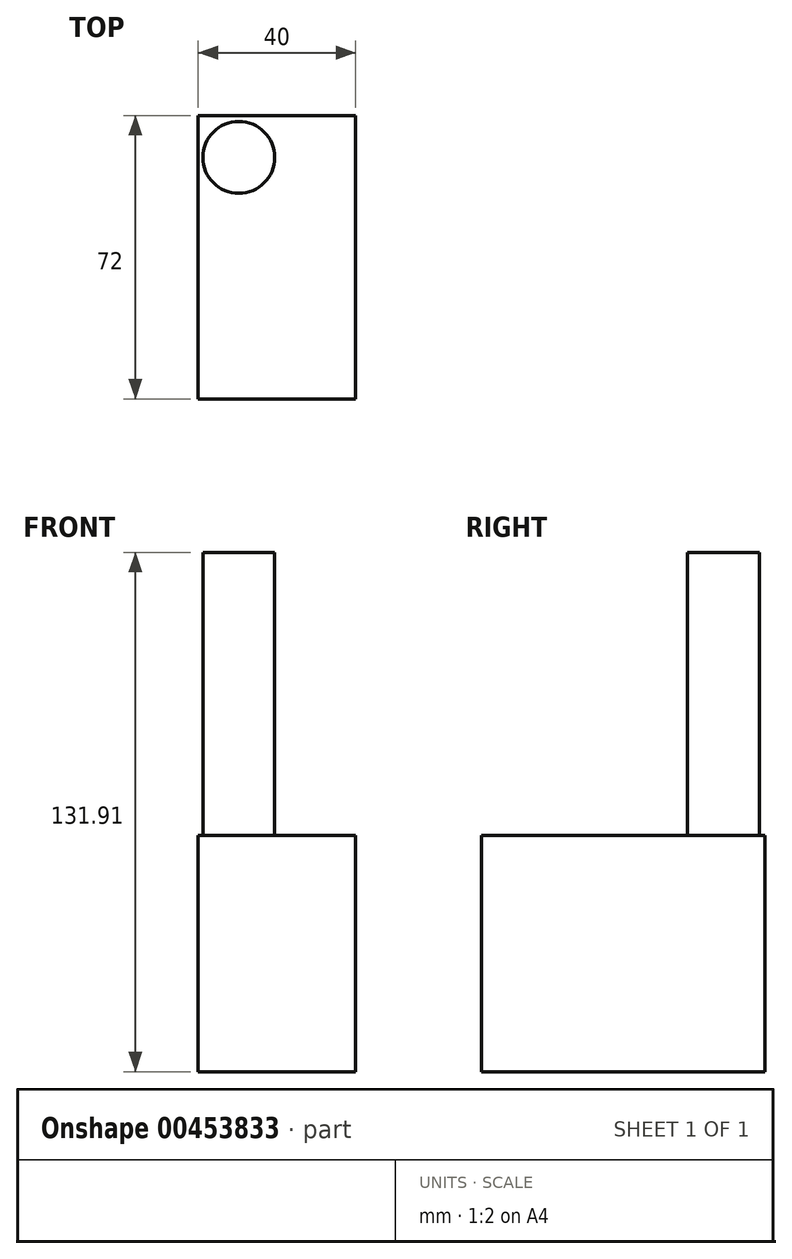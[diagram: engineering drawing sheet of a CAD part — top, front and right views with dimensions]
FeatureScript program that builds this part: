
annotation { "Feature Type Name" : "Feature", "Feature Type Description" : "" }
export const myFeature = defineFeature(function(context is Context, id is Id, definition is map)
    precondition{}
    {
        {
            var Q0;
            Q0=qCreatedBy(makeId("Front.planeOp"),FACE);
            var sketch = newSketch(context, id + "F0", { "sketchPlane" : qUnion([Q0])});
            skLineSegment(sketch, "E0.bottom", {"start": v(-20, 30) * mm, "end": v(20, 30) * mm});
            skLineSegment(sketch, "E0.top", {"start": v(-20, -30) * mm, "end": v(20, -30) * mm});
            skLineSegment(sketch, "E0.left", {"start": v(-20, 30) * mm, "end": v(-20, -30) * mm});
            skLineSegment(sketch, "E0.right", {"start": v(20, 30) * mm, "end": v(20, -30) * mm});
            skPoint(sketch, "E0.middle", {"position": v(0, 0) * mm});
            skSolve(sketch);
        }
        {
            var Q0;
            Q0=makeQuery(id+"F0.imprint","IMPRINT",FACE,{"disambiguationData":[TD([[makeQuery(id+"F0.imprint","IMPRINT",EDGE,{"derivedFrom":sQuery(id+"F0.wireOp",EDGE,"E0.bottom")}),-1.0]])]});
            extrude(context, id + "F1", {"entities" : qUnion([Q0]), "endBound" : BoundingType.SYMMETRIC, "depth" : 72 * mm});
        }
        {
            var Q0;
            Q0=qCreatedBy(makeId("Top.planeOp"),FACE);
            var sketch = newSketch(context, id + "F2", { "sketchPlane" : qUnion([Q0])});
            skCircle(sketch, "E1", {"center": v(-9.7, 25.38) * mm, "radius": 9.13 * mm});
            skSolve(sketch);
        }
        {
            var Q0;
            Q0 = qSketchRegion(id + "F2", true);
            extrude(context, id + "F3", {"entities" : qUnion([Q0]), "operationType" : NewBodyOperationType.ADD, "endBound" : BoundingType.THROUGH_ALL, "depth" : 80 * mm});
        }
    });
